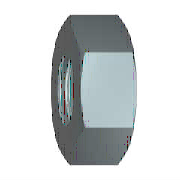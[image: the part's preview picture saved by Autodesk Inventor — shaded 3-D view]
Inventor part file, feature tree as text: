
AUTODESK INVENTOR PART (.ipt)
format: ipt  version: 2018.1 (Build 221171000, 171)  size: 162,816 bytes
history: native  units: mm (DEFAULTED — no unit token found)
features: sketch x3, chamfer x1, hole x1, other x1, plane x1
ambient origin geometry x7: Origin, YZ Plane, XZ Plane, X Axis, Y Axis, Z Axis, Center Point
bodies: Solid1 (feature_tree), Body (feature_tree)
feature tree (7):
  chamfer  "Chamfer1"  Angle=30.0deg  [1 undecoded]
  hole  "Thread"  [1 undecoded]
  other  "Work Axis1"
  plane  "Work Plane1"
  sketch  "Sketch1"  dims[d0=21.93931mm]
  sketch  "Sketch2"  dims[d1=10.0mm]
  sketch  "Sketch3"  dims[d2=0.0mm d3=30.0deg d4=30.0deg d5=17.2mm d6=17.2mm d7=90.0deg d25=10.106mm d26=6.0mm d27=4.0mm d28=2.0mm d29=14.3117mm d30=8.0mm d31=20.594885mm d8=0.947215mm d9=30.0deg d10=0.947215mm d11=30.0deg d13=0.0mm d14=0.0mm d39=0.0mm d40=0.947215mm d41=0.947215mm d42=0.0mm]
note: 2 required parameter values undecoded (feature->parameter linkage not recoverable at this tier; creation-order binding heuristic only, values carry confidence <= 0.55)
